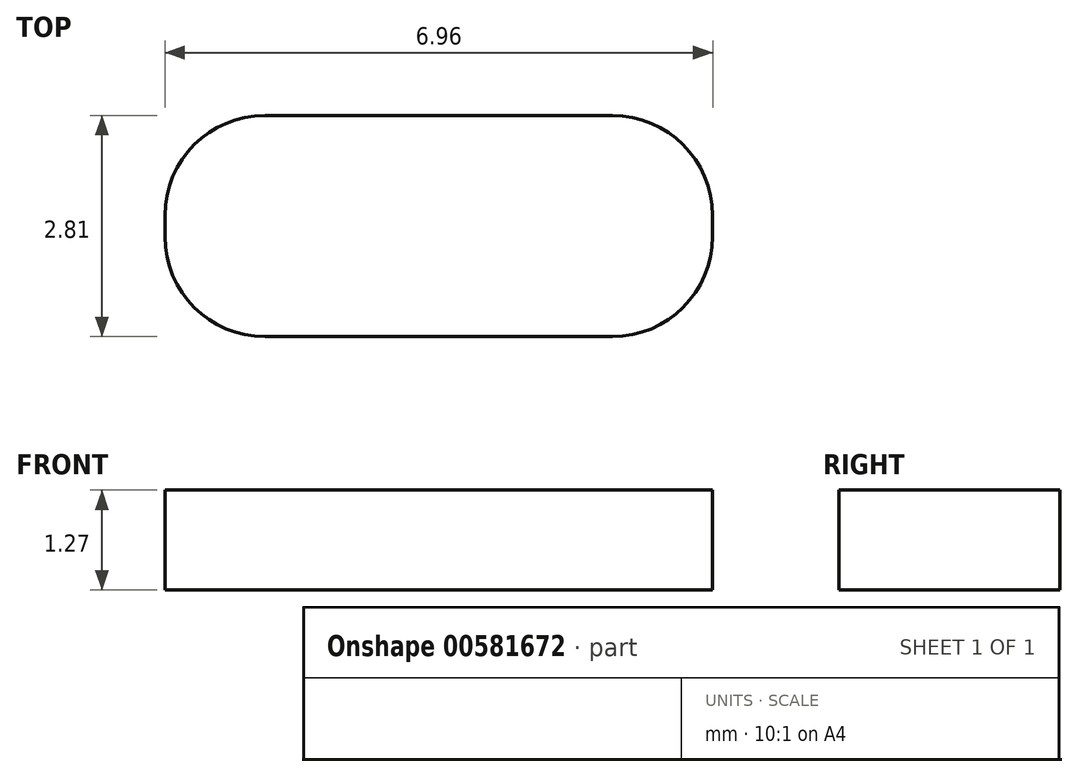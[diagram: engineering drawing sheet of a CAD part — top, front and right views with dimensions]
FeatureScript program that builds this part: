
annotation { "Feature Type Name" : "Feature", "Feature Type Description" : "" }
export const myFeature = defineFeature(function(context is Context, id is Id, definition is map)
    precondition{}
    {
        {
            var Q0;
            Q0=qCreatedBy(makeId("Top.planeOp"),FACE);
            var sketch = newSketch(context, id + "F0", { "sketchPlane" : qUnion([Q0])});
            skLineSegment(sketch, "E0.bottom", {"start": v(1.27, 0) * mm, "end": v(5.69, 0) * mm});
            skLineSegment(sketch, "E0.top", {"start": v(1.27, 2.8) * mm, "end": v(5.69, 2.8) * mm});
            skLineSegment(sketch, "E0.left", {"start": v(0, 1.27) * mm, "end": v(0, 1.54) * mm});
            skLineSegment(sketch, "E0.right", {"start": v(6.96, 1.27) * mm, "end": v(6.96, 1.54) * mm});
            skPoint(sketch, "E1.visualSharp", {"position": v(0, 2.8) * mm});
            skArc(sketch, "E1.filletArc", {"start": v(1.27, 2.8) * mm, "mid": v(0.37, 2.44) * mm, "end": v(0, 1.54) * mm});
            skPoint(sketch, "E2.visualSharp", {"position": v(6.96, 0) * mm});
            skArc(sketch, "E2.filletArc", {"start": v(5.69, 0) * mm, "mid": v(6.58, 0.37) * mm, "end": v(6.96, 1.27) * mm});
            skPoint(sketch, "E3.visualSharp", {"position": v(6.96, 2.8) * mm});
            skArc(sketch, "E3.filletArc", {"start": v(6.96, 1.54) * mm, "mid": v(6.58, 2.44) * mm, "end": v(5.69, 2.8) * mm});
            skPoint(sketch, "E4.visualSharp", {"position": v(0, 0) * mm});
            skArc(sketch, "E4.filletArc", {"start": v(0, 1.27) * mm, "mid": v(0.37, 0.37) * mm, "end": v(1.27, 0) * mm});
            skSolve(sketch);
        }
        {
            var Q0;
            Q0 = qSketchRegion(id + "F0", true);
            extrude(context, id + "F1", {"entities" : qUnion([Q0]), "depth" : 1.27 * mm, "offsetDistance" : 25.4 * mm});
        }
        {
            var Q0;
            Q0=makeQuery(id+"F1.opExtrude","SWEPT_BODY",BODY,{"disambiguationData":[OSD([sQuery(id+"F0.wireOp",EDGE,"E0.bottom"),sQuery(id+"F0.wireOp",EDGE,"E0.top"),sQuery(id+"F0.wireOp",EDGE,"E0.left"),sQuery(id+"F0.wireOp",EDGE,"E0.right"),sQuery(id+"F0.wireOp",EDGE,"E1.filletArc"),sQuery(id+"F0.wireOp",EDGE,"E2.filletArc"),sQuery(id+"F0.wireOp",EDGE,"E3.filletArc"),sQuery(id+"F0.wireOp",EDGE,"E4.filletArc")])]});
            transform(context, id + "F2", {"entities" : qUnion([Q0]), "transformType" : TransformType.TRANSLATION_3D, "dx" : 9.37 * mm, "dy" : 0 * mm, "dz" : 0.05 * mm, "makeCopy" : true});
        }
        {
            var Q0;
            Q0=makeQuery(id+"F2.opPattern","COPY",BODY,{"derivedFrom":makeQuery(id+"F1.opExtrude","SWEPT_BODY",BODY,{"disambiguationData":[OSD([sQuery(id+"F0.wireOp",EDGE,"E0.bottom"),sQuery(id+"F0.wireOp",EDGE,"E0.top"),sQuery(id+"F0.wireOp",EDGE,"E0.left"),sQuery(id+"F0.wireOp",EDGE,"E0.right"),sQuery(id+"F0.wireOp",EDGE,"E1.filletArc"),sQuery(id+"F0.wireOp",EDGE,"E2.filletArc"),sQuery(id+"F0.wireOp",EDGE,"E3.filletArc"),sQuery(id+"F0.wireOp",EDGE,"E4.filletArc")])]}),"instanceName":"1"});
            deleteBodies(context, id + "F3", {"entities" : qUnion([Q0])});
        }
    });
